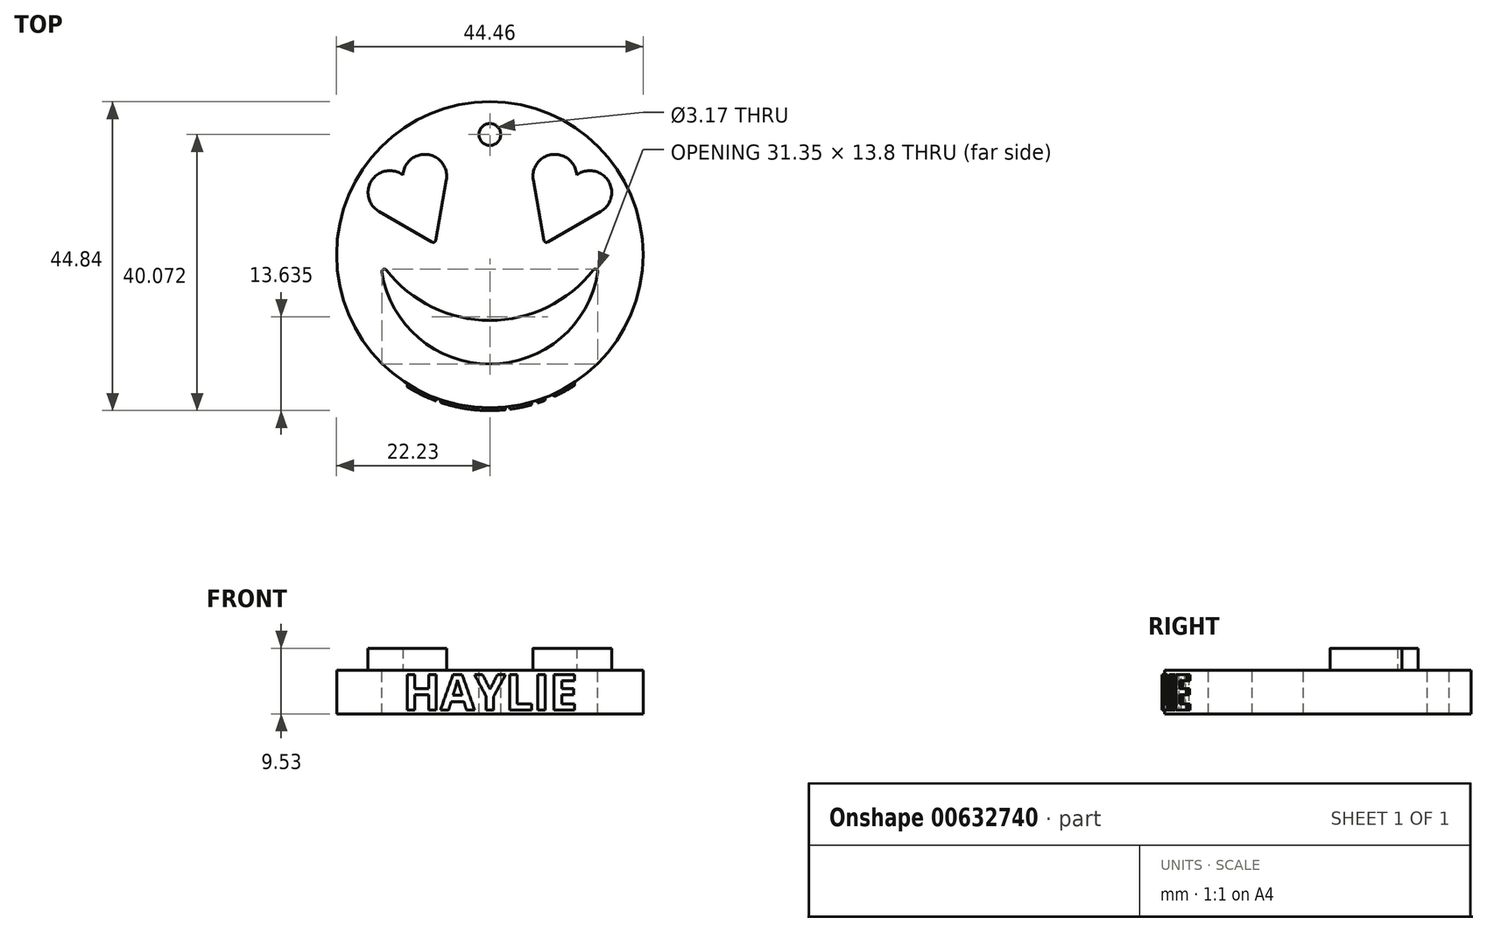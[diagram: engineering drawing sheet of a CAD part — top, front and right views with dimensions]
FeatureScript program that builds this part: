
annotation { "Feature Type Name" : "Feature", "Feature Type Description" : "" }
export const myFeature = defineFeature(function(context is Context, id is Id, definition is map)
    precondition{}
    {
        {
            var Q0;
            Q0=qCreatedBy(makeId("Top.planeOp"),FACE);
            var sketch = newSketch(context, id + "F0", { "sketchPlane" : qUnion([Q0])});
            skCircle(sketch, "E0", {"center": v(0, 0) * mm, "radius": 22.23 * mm});
            skSolve(sketch);
        }
        {
            var Q0;
            Q0 = qSketchRegion(id + "F0", true);
            extrude(context, id + "F1", {"entities" : qUnion([Q0]), "depth" : 6.35 * mm, "offsetDistance" : 25.4 * mm});
        }
        {
            var Q0;
            Q0=makeQuery(id+"F1.opExtrude","CAP_FACE",FACE,{"disambiguationData":[OSD([sQuery(id+"F0.wireOp",EDGE,"E0")])],"isStart":false});
            var sketch = newSketch(context, id + "F2", { "sketchPlane" : qUnion([Q0])});
            skLineSegment(sketch, "E1", {"start": v(-7.94, 1.59) * mm, "end": v(-6.3, 10.85) * mm});
            skLineSegment(sketch, "E2", {"start": v(-7.94, 1.59) * mm, "end": v(-16.08, 6.29) * mm});
            skLineSegment(sketch, "E3", {"start": v(0, 22.23) * mm, "end": v(0, -22.23) * mm, "construction": true});
            skLineSegment(sketch, "E4", {"start": v(-11.96, 10.22) * mm, "end": v(-7.94, 1.59) * mm, "construction": true});
            skLineSegment(sketch, "E5", {"start": v(-9.43, 11.4) * mm, "end": v(-14.5, 9.04) * mm, "construction": true});
            skArc(sketch, "E6", {"start": v(-12.6, 11.59) * mm, "mid": v(-17.15, 10.78) * mm, "end": v(-16.08, 6.29) * mm});
            skArc(sketch, "E7", {"start": v(-6.3, 10.85) * mm, "mid": v(-9.06, 14.55) * mm, "end": v(-12.6, 11.59) * mm});
            skArc(sketch, "E8.MirrorCS", {"start": v(12.6, 11.59) * mm, "mid": v(17.15, 10.78) * mm, "end": v(16.08, 6.29) * mm});
            skLineSegment(sketch, "E9.MirrorCS", {"start": v(11.96, 10.22) * mm, "end": v(7.94, 1.59) * mm, "construction": true});
            skLineSegment(sketch, "E10.MirrorCS", {"start": v(7.94, 1.59) * mm, "end": v(6.3, 10.85) * mm});
            skLineSegment(sketch, "E11.MirrorCS", {"start": v(9.43, 11.4) * mm, "end": v(14.5, 9.04) * mm, "construction": true});
            skLineSegment(sketch, "E12.MirrorCS", {"start": v(7.94, 1.59) * mm, "end": v(16.08, 6.29) * mm});
            skArc(sketch, "E13.MirrorCS", {"start": v(6.3, 10.85) * mm, "mid": v(9.06, 14.55) * mm, "end": v(12.6, 11.59) * mm});
            skSolve(sketch);
        }
        {
            var Q0;
            Q0 = qSketchRegion(id + "F2", true);
            extrude(context, id + "F3", {"entities" : qUnion([Q0]), "operationType" : NewBodyOperationType.ADD, "depth" : 3.17 * mm, "offsetDistance" : 25.4 * mm});
        }
        {
            var Q0;
            Q0=makeQuery(id+"F1.opExtrude","CAP_FACE",FACE,{"disambiguationData":[OSD([sQuery(id+"F0.wireOp",EDGE,"E0")])],"isStart":false});
            var sketch = newSketch(context, id + "F4", { "sketchPlane" : qUnion([Q0])});
            skArc(sketch, "E14", {"start": v(-15.84, -1.06) * mm, "mid": v(0, -15.88) * mm, "end": v(15.84, -1.06) * mm});
            skLineSegment(sketch, "E15", {"start": v(0, 0) * mm, "end": v(0, -22.23) * mm, "construction": true});
            skArc(sketch, "E16", {"start": v(-15.84, -1.06) * mm, "mid": v(0, -9.53) * mm, "end": v(15.84, -1.06) * mm});
            skCircle(sketch, "E17", {"center": v(0, 17.46) * mm, "radius": 1.59 * mm});
            skSolve(sketch);
        }
        {
            var Q0;
            Q0=makeQuery(id+"F4.imprint","IMPRINT",FACE,{"disambiguationData":[TD([[makeQuery(id+"F4.imprint","IMPRINT",EDGE,{"derivedFrom":sQuery(id+"F4.wireOp",EDGE,"E14")}),1.0]])]});
            var Q1;
            Q1=makeQuery(id+"F4.imprint","IMPRINT",FACE,{"disambiguationData":[TD([[makeQuery(id+"F4.imprint","IMPRINT",EDGE,{"derivedFrom":sQuery(id+"F4.wireOp",EDGE,"E17")}),1.0]])]});
            extrude(context, id + "F5", {"entities" : qUnion([Q0, Q1]), "operationType" : NewBodyOperationType.REMOVE, "endBound" : BoundingType.THROUGH_ALL, "oppositeDirection" : true, "depth" : 25.4 * mm, "offsetDistance" : 25.4 * mm});
        }
        {
            var Q0;
            Q0=makeQuery(id+"F3.opExtrude","SWEPT_EDGE",EDGE,{"disambiguationData":[OSD([sQuery(id+"F2.wireOp",EDGE,"E1"),sQuery(id+"F2.wireOp",EDGE,"E2")])]});
            var Q1;
            Q1=makeQuery(id+"F3.opExtrude","SWEPT_EDGE",EDGE,{"disambiguationData":[OSD([sQuery(id+"F2.wireOp",EDGE,"E10.MirrorCS"),sQuery(id+"F2.wireOp",EDGE,"E12.MirrorCS")])]});
            var Q2;
            {var subQ0=sQuery(id+"F4.wireOp",EDGE,"E16");var subQ1=sQuery(id+"F4.wireOp",EDGE,"E14");Q2=makeQuery(id+"F5.boolean.opBoolean","COPY",EDGE,{"derivedFrom":makeQuery(id+"F5.opExtrude","SWEPT_EDGE",EDGE,{"disambiguationData":[OSD([subQ1,subQ0]),TDD([makeQuery(id+"F4.imprint","INTERSECT",VERTEX,{"disambiguationData":[OD(1.0)],"derivedFrom":[subQ1,subQ0]})])]})});}
            var Q3;
            {var subQ0=sQuery(id+"F4.wireOp",EDGE,"E16");var subQ1=sQuery(id+"F4.wireOp",EDGE,"E14");Q3=makeQuery(id+"F5.boolean.opBoolean","COPY",EDGE,{"derivedFrom":makeQuery(id+"F5.opExtrude","SWEPT_EDGE",EDGE,{"disambiguationData":[OSD([subQ1,subQ0]),TDD([makeQuery(id+"F4.imprint","INTERSECT",VERTEX,{"disambiguationData":[OD(0.0)],"derivedFrom":[subQ1,subQ0]})])]})});}
            fillet(context, id + "F6", {"entities" : qUnion([Q0, Q1, Q2, Q3]), "radius" : 0.38 * mm, "tangentPropagation" : true, "allowEdgeOverflow" : false});
        }
        {
            var Q0;
            Q0=qCreatedBy(makeId("Front.planeOp"),FACE);
            cPlane(context, id + "F7", {"entities" : qUnion([Q0]), "cplaneType" : CPlaneType.OFFSET, "offset" : 22.6 * mm, "width" : 152.4 * mm, "height" : 152.4 * mm});
        }
        {
            var Q0;
            Q0=qCreatedBy(id+"F7.planeOp",FACE);
            var sketch = newSketch(context, id + "F8", { "sketchPlane" : qUnion([Q0])});
            skText(sketch, "E18", { "text": "HAYLIE", "fontName": "OpenSans-Bold.ttf"});
            const initialGuessF8  = {"E18": [-0.01264, 0.00056, 1, 0, 0.00516]};
            skSetInitialGuess(sketch, initialGuessF8);
            skSolve(sketch);
        }
        {
            var Q0;
            Q0 = qSketchRegion(id + "F8", true);
            var Q1;
            Q1=makeQuery(id+"F1.opExtrude","SWEPT_FACE",FACE,{"disambiguationData":[OSD([sQuery(id+"F0.wireOp",EDGE,"E0")])]});
            var Q2;
            Q2=makeQuery(id+"F1.opExtrude","SWEPT_BODY",BODY,{"disambiguationData":[OSD([sQuery(id+"F0.wireOp",EDGE,"E0")])]});
            extrude(context, id + "F9", {"entities" : qUnion([Q0]), "operationType" : NewBodyOperationType.ADD, "oppositeDirection" : true, "depth" : 4.44 * mm, "endBoundEntityFace" : qUnion([Q1]), "endBoundEntityBody" : qUnion([Q2]), "offsetDistance" : 25.4 * mm});
        }
        {
            var Q0;
            Q0=makeQuery(id+"F1.opExtrude","CAP_FACE",FACE,{"disambiguationData":[OSD([sQuery(id+"F0.wireOp",EDGE,"E0")])],"isStart":false});
            var sketch = newSketch(context, id + "F10", { "sketchPlane" : qUnion([Q0])});
            skLineSegment(sketch, "E19", {"start": v(-13.15, -18.39) * mm, "end": v(-13.15, -36) * mm});
            skLineSegment(sketch, "E20", {"start": v(-13.15, -36) * mm, "end": v(16.3, -36) * mm});
            skLineSegment(sketch, "E21", {"start": v(16.3, -36) * mm, "end": v(16.3, -15.66) * mm});
            skArc(sketch, "E22", {"start": v(-13.15, -18.39) * mm, "mid": v(2.08, -22.5) * mm, "end": v(16.3, -15.66) * mm});
            skSolve(sketch);
        }
        {
            var Q0;
            Q0 = qSketchRegion(id + "F10", true);
            extrude(context, id + "F11", {"entities" : qUnion([Q0]), "operationType" : NewBodyOperationType.REMOVE, "endBound" : BoundingType.THROUGH_ALL, "oppositeDirection" : true, "depth" : 25.4 * mm, "offsetDistance" : 25.4 * mm});
        }
    });
